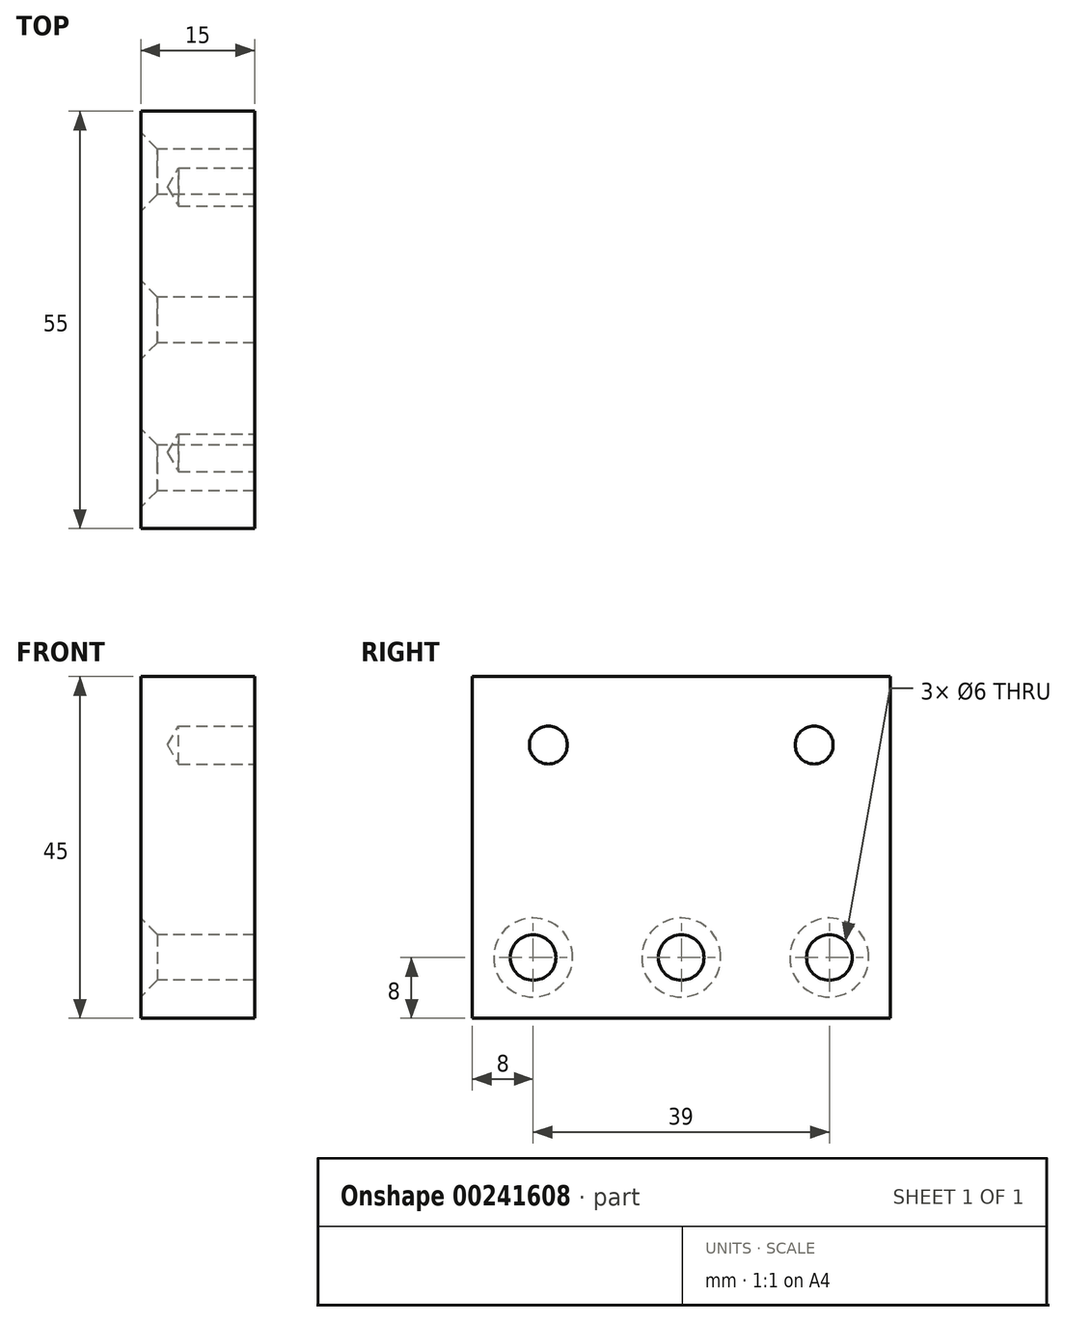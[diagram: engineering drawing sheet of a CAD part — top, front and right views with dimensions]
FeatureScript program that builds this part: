
annotation { "Feature Type Name" : "Feature", "Feature Type Description" : "" }
export const myFeature = defineFeature(function(context is Context, id is Id, definition is map)
    precondition{}
    {
        {
            var Q0;
            Q0=qCreatedBy(makeId("Right.planeOp"),FACE);
            var sketch = newSketch(context, id + "F0", { "sketchPlane" : qUnion([Q0])});
            skLineSegment(sketch, "E0.bottom", {"start": v(27.5, 22.5) * mm, "end": v(-27.5, 22.5) * mm});
            skLineSegment(sketch, "E0.top", {"start": v(27.5, -22.5) * mm, "end": v(-27.5, -22.5) * mm});
            skLineSegment(sketch, "E0.left", {"start": v(27.5, 22.5) * mm, "end": v(27.5, -22.5) * mm});
            skLineSegment(sketch, "E0.right", {"start": v(-27.5, 22.5) * mm, "end": v(-27.5, -22.5) * mm});
            skPoint(sketch, "E0.middle", {"position": v(0, 0) * mm});
            skSolve(sketch);
        }
        {
            var Q0;
            Q0 = qSketchRegion(id + "F0", true);
            extrude(context, id + "F1", {"entities" : qUnion([Q0]), "depth" : 15 * mm});
        }
        {
            var Q0;
            Q0=makeQuery(id+"F1.opExtrude","CAP_FACE",FACE,{"disambiguationData":[OSD([sQuery(id+"F0.wireOp",EDGE,"E0.bottom"),sQuery(id+"F0.wireOp",EDGE,"E0.top"),sQuery(id+"F0.wireOp",EDGE,"E0.left"),sQuery(id+"F0.wireOp",EDGE,"E0.right")])],"isStart":false});
            var sketch = newSketch(context, id + "F2", { "sketchPlane" : qUnion([Q0])});
            skPoint(sketch, "E1", {"position": v(-17.5, 13.5) * mm});
            skPoint(sketch, "E2", {"position": v(17.5, 13.5) * mm});
            skSolve(sketch);
        }
        {
            var Q0;
            Q0=makeQuery(id+"F1.opExtrude","CAP_FACE",FACE,{"disambiguationData":[OSD([sQuery(id+"F0.wireOp",EDGE,"E0.bottom"),sQuery(id+"F0.wireOp",EDGE,"E0.top"),sQuery(id+"F0.wireOp",EDGE,"E0.left"),sQuery(id+"F0.wireOp",EDGE,"E0.right")])],"isStart":true});
            var sketch = newSketch(context, id + "F3", { "sketchPlane" : qUnion([Q0])});
            skPoint(sketch, "E3", {"position": v(-19.5, -14.5) * mm});
            skPoint(sketch, "E4", {"position": v(0, -14.5) * mm});
            skPoint(sketch, "E5", {"position": v(19.5, -14.5) * mm});
            skSolve(sketch);
        }
        {
            var Q0;
            Q0=sQuery(id+"F3.wireOp",VERTEX,"E3");
            var Q1;
            Q1=sQuery(id+"F3.wireOp",VERTEX,"E4");
            var Q2;
            Q2=sQuery(id+"F3.wireOp",VERTEX,"E5");
            var Q3;
            Q3=makeQuery(id+"F1.opExtrude","SWEPT_BODY",BODY,{"disambiguationData":[OSD([sQuery(id+"F0.wireOp",EDGE,"E0.bottom"),sQuery(id+"F0.wireOp",EDGE,"E0.top"),sQuery(id+"F0.wireOp",EDGE,"E0.left"),sQuery(id+"F0.wireOp",EDGE,"E0.right")])]});
            hole(context, id + "F4", {"style" : HoleStyle.C_SINK, "endStyle" : HoleEndStyle.BLIND, "holeDiameter" : 6 * mm, "cSinkDiameter" : 10.4 * mm, "cSinkAngle" : 90 * degree, "holeDepth" : 15 * mm, "startFromSketch" : true, "locations" : qUnion([Q0, Q1, Q2]), "scope" : qUnion([Q3])});
        }
        {
            var Q0;
            Q0=sQuery(id+"F2.wireOp",VERTEX,"E1");
            var Q1;
            Q1=sQuery(id+"F2.wireOp",VERTEX,"E2");
            var Q2;
            Q2=makeQuery(id+"F1.opExtrude","SWEPT_BODY",BODY,{"disambiguationData":[OSD([sQuery(id+"F0.wireOp",EDGE,"E0.bottom"),sQuery(id+"F0.wireOp",EDGE,"E0.top"),sQuery(id+"F0.wireOp",EDGE,"E0.left"),sQuery(id+"F0.wireOp",EDGE,"E0.right")])]});
            hole(context, id + "F5", {"style" : HoleStyle.SIMPLE, "endStyle" : HoleEndStyle.BLIND, "holeDiameter" : 5 * mm, "holeDepth" : 10 * mm, "startFromSketch" : true, "locations" : qUnion([Q0, Q1]), "scope" : qUnion([Q2])});
        }
    });
